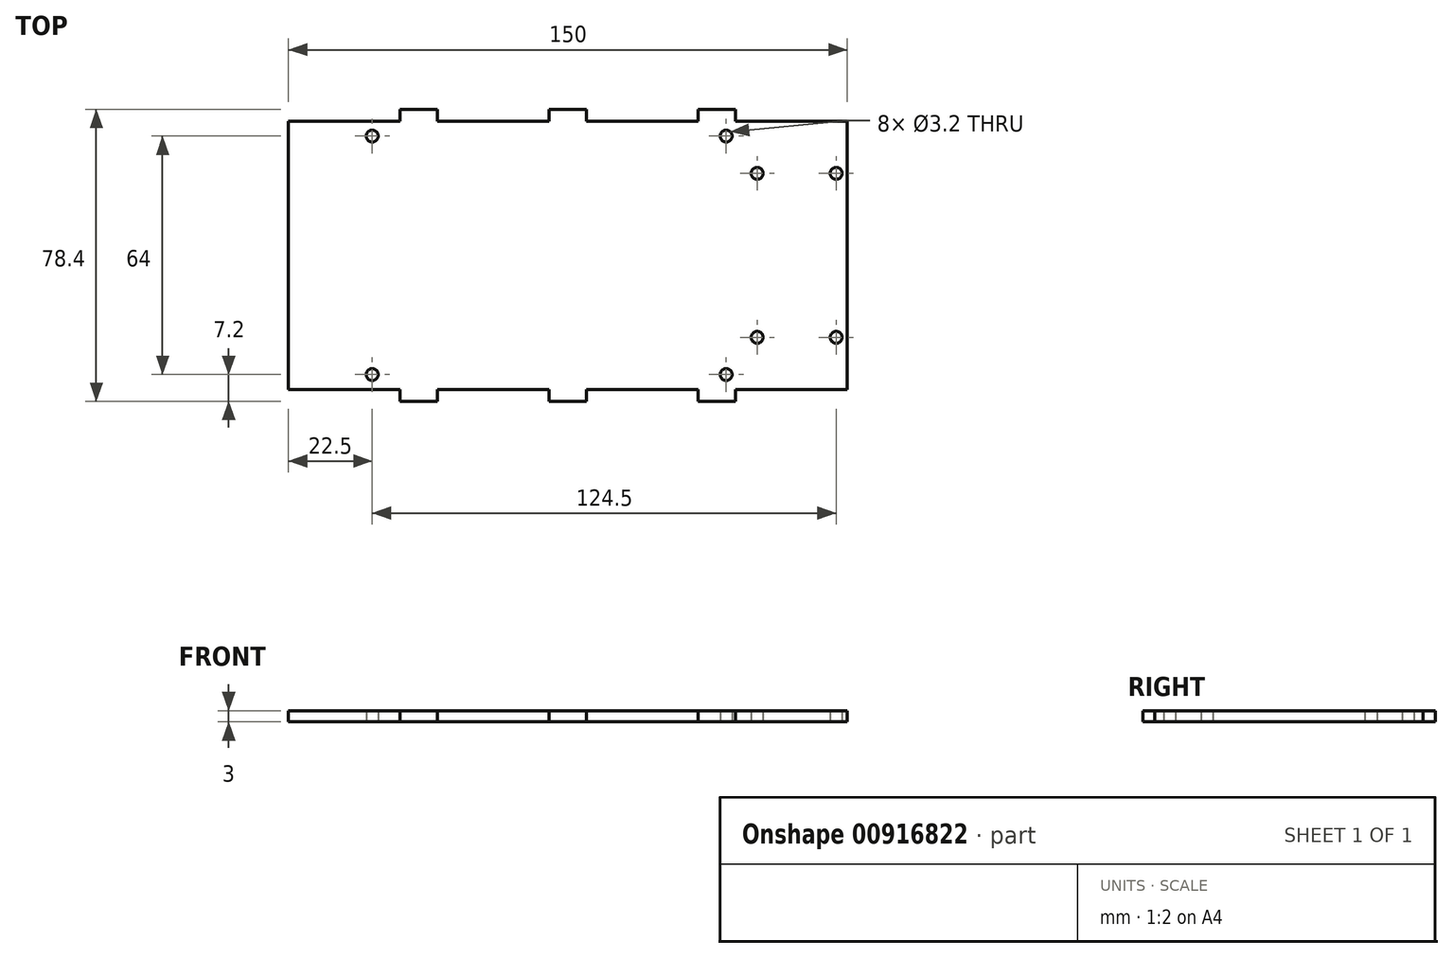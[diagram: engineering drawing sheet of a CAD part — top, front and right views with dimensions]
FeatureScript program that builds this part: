
annotation { "Feature Type Name" : "Feature", "Feature Type Description" : "" }
export const myFeature = defineFeature(function(context is Context, id is Id, definition is map)
    precondition{}
    {
        {
            var Q0;
            Q0=qCreatedBy(makeId("Top.planeOp"),FACE);
            var sketch = newSketch(context, id + "F0", { "sketchPlane" : qUnion([Q0])});
            skLineSegment(sketch, "E0.bottom", {"start": v(-75, 36) * mm, "end": v(-45, 36) * mm});
            skLineSegment(sketch, "E0.top", {"start": v(-75, -36) * mm, "end": v(-45, -36) * mm});
            skLineSegment(sketch, "E0.left", {"start": v(-75, 36) * mm, "end": v(-75, -36) * mm});
            skLineSegment(sketch, "E0.right", {"start": v(75, 36) * mm, "end": v(75, -36) * mm});
            skLineSegment(sketch, "E1", {"start": v(0, 36) * mm, "end": v(0, -36) * mm, "construction": true});
            skLineSegment(sketch, "E2", {"start": v(-75, 0) * mm, "end": v(75, 0) * mm, "construction": true});
            skLineSegment(sketch, "E3.top", {"start": v(-45, 39.2) * mm, "end": v(-35, 39.2) * mm});
            skLineSegment(sketch, "E3.left", {"start": v(-45, 36) * mm, "end": v(-45, 39.2) * mm});
            skLineSegment(sketch, "E3.right", {"start": v(-35, 36) * mm, "end": v(-35, 39.2) * mm});
            skLineSegment(sketch, "E4.MirrorCS", {"start": v(35, 36) * mm, "end": v(35, 39.2) * mm});
            skLineSegment(sketch, "E5.MirrorCS", {"start": v(45, 36) * mm, "end": v(45, 39.2) * mm});
            skLineSegment(sketch, "E6.MirrorCS", {"start": v(45, 39.2) * mm, "end": v(35, 39.2) * mm});
            skLineSegment(sketch, "E7.trimOffspring", {"start": v(-35, 36) * mm, "end": v(-5.53, 36) * mm});
            skLineSegment(sketch, "E8.trimOffspring", {"start": v(5.53, 36) * mm, "end": v(35, 36) * mm});
            skLineSegment(sketch, "E9.trimOffspring", {"start": v(45, 36) * mm, "end": v(75, 36) * mm});
            skLineSegment(sketch, "E10.MirrorCS", {"start": v(-45, -36) * mm, "end": v(-45, -39.2) * mm});
            skLineSegment(sketch, "E11.MirrorCS", {"start": v(35, -36) * mm, "end": v(35, -39.2) * mm});
            skLineSegment(sketch, "E12.MirrorCS", {"start": v(45, -36) * mm, "end": v(45, -39.2) * mm});
            skLineSegment(sketch, "E13.MirrorCS", {"start": v(-35, -36) * mm, "end": v(-35, -39.2) * mm});
            skLineSegment(sketch, "E14.MirrorCS", {"start": v(-45, -39.2) * mm, "end": v(-35, -39.2) * mm});
            skLineSegment(sketch, "E15.MirrorCS", {"start": v(45, -39.2) * mm, "end": v(35, -39.2) * mm});
            skLineSegment(sketch, "E16.MirrorCS", {"start": v(-35, -36) * mm, "end": v(-5.53, -36) * mm});
            skLineSegment(sketch, "E17.MirrorCS", {"start": v(5.53, -36) * mm, "end": v(35, -36) * mm});
            skLineSegment(sketch, "E18.trimOffspring", {"start": v(45, -36) * mm, "end": v(75, -36) * mm});
            skCircle(sketch, "E19", {"center": v(-52.5, 32) * mm, "radius": 1.6 * mm});
            skLineSegment(sketch, "E20", {"start": v(-52.5, 32) * mm, "end": v(75, 32) * mm, "construction": true});
            skCircle(sketch, "E21", {"center": v(42.5, 32) * mm, "radius": 1.6 * mm});
            skCircle(sketch, "E22.MirrorC", {"center": v(-52.5, -32) * mm, "radius": 1.6 * mm});
            skCircle(sketch, "E23.MirrorC", {"center": v(42.5, -32) * mm, "radius": 1.6 * mm});
            skCircle(sketch, "E24", {"center": v(72, 22) * mm, "radius": 1.6 * mm});
            skLineSegment(sketch, "E25", {"start": v(72, 22) * mm, "end": v(-75, 22) * mm, "construction": true});
            skCircle(sketch, "E26", {"center": v(50.8, 22) * mm, "radius": 1.6 * mm});
            skCircle(sketch, "E27.MirrorC", {"center": v(72, -22) * mm, "radius": 1.6 * mm});
            skCircle(sketch, "E28.MirrorC", {"center": v(50.8, -22) * mm, "radius": 1.6 * mm});
            skLineSegment(sketch, "E29", {"start": v(-5.53, 36) * mm, "end": v(-5, 36) * mm});
            skLineSegment(sketch, "E30.top", {"start": v(-5, 39.2) * mm, "end": v(5, 39.2) * mm});
            skLineSegment(sketch, "E30.left", {"start": v(-5, 36) * mm, "end": v(-5, 39.2) * mm});
            skLineSegment(sketch, "E30.right", {"start": v(5, 36) * mm, "end": v(5, 39.2) * mm});
            skLineSegment(sketch, "E31.trimOffspring", {"start": v(5, 36) * mm, "end": v(5.53, 36) * mm});
            skLineSegment(sketch, "E32", {"start": v(-5.53, -36) * mm, "end": v(-5, -36) * mm});
            skLineSegment(sketch, "E33.MirrorCS", {"start": v(5, -36) * mm, "end": v(5, -39.2) * mm});
            skLineSegment(sketch, "E34.MirrorCS", {"start": v(-5, -36) * mm, "end": v(-5, -39.2) * mm});
            skLineSegment(sketch, "E35.MirrorCS", {"start": v(-5, -39.2) * mm, "end": v(5, -39.2) * mm});
            skLineSegment(sketch, "E36.trimOffspring", {"start": v(5, -36) * mm, "end": v(5.53, -36) * mm});
            skSolve(sketch);
        }
        {
            var Q0;
            Q0 = qSketchRegion(id + "F0", true);
            extrude(context, id + "F1", {"entities" : qUnion([Q0]), "depth" : 3 * mm, "offsetDistance" : 25 * mm});
        }
    });
